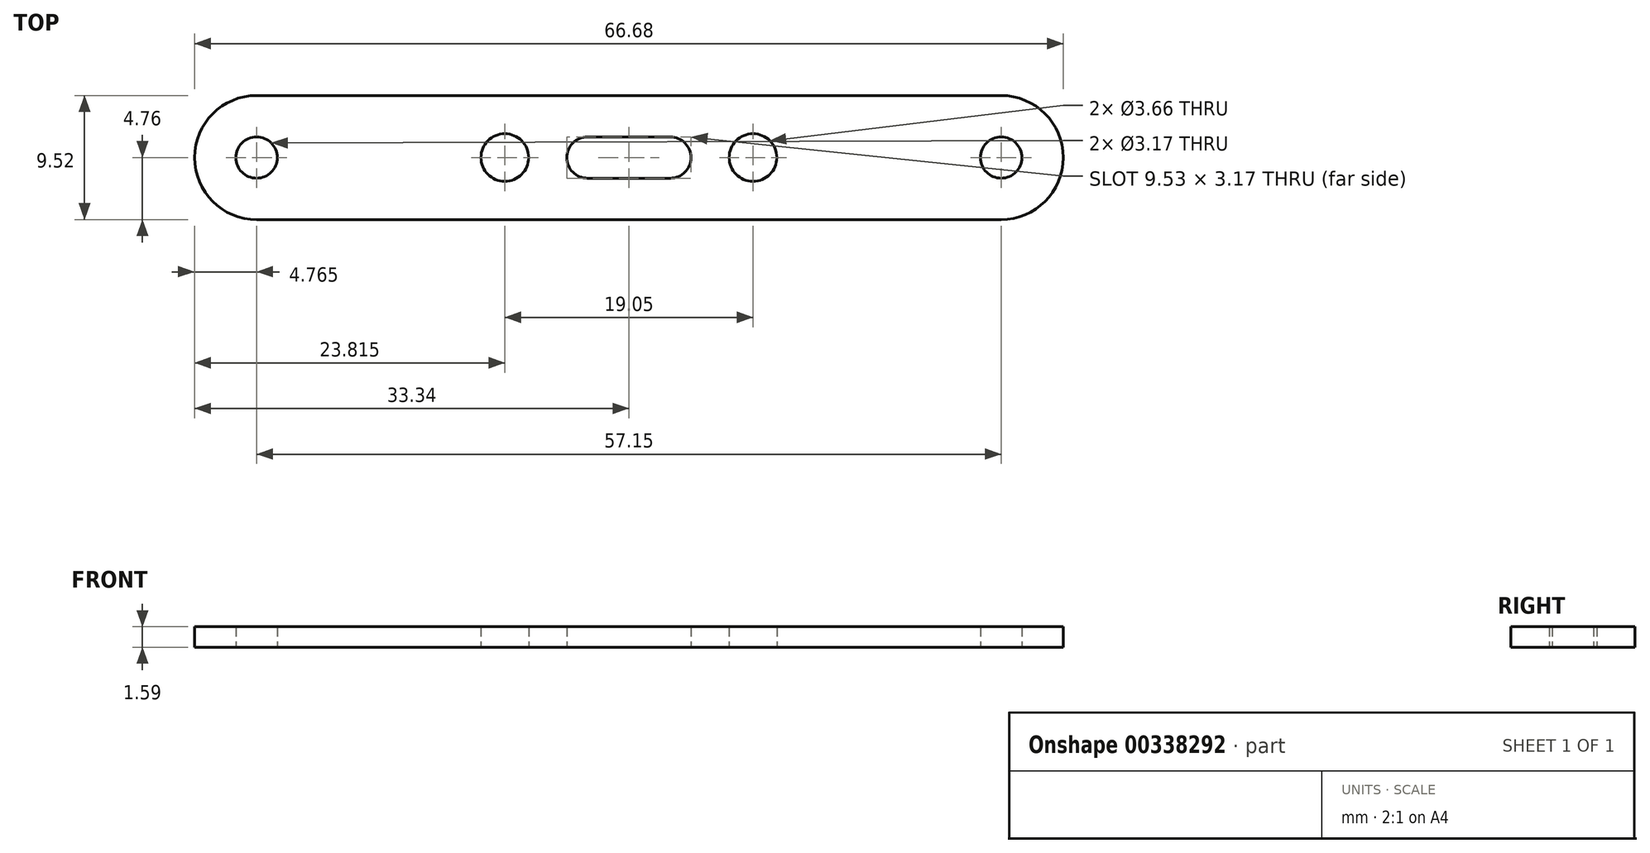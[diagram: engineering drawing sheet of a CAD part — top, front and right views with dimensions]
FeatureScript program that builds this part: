
annotation { "Feature Type Name" : "Feature", "Feature Type Description" : "" }
export const myFeature = defineFeature(function(context is Context, id is Id, definition is map)
    precondition{}
    {
        {
            var Q0;
            Q0=qCreatedBy(makeId("Top.planeOp"),FACE);
            var sketch = newSketch(context, id + "F0", { "sketchPlane" : qUnion([Q0])});
            skLineSegment(sketch, "E0.bottom", {"start": v(3.18, -1.59) * mm, "end": v(-3.18, -1.59) * mm});
            skLineSegment(sketch, "E0.top", {"start": v(3.18, 1.59) * mm, "end": v(-3.18, 1.59) * mm});
            skLineSegment(sketch, "E0.left", {"start": v(3.18, -1.59) * mm, "end": v(3.18, 1.59) * mm, "construction": true});
            skLineSegment(sketch, "E0.right", {"start": v(-3.18, -1.59) * mm, "end": v(-3.18, 1.59) * mm, "construction": true});
            skPoint(sketch, "E0.middle", {"position": v(0, 0) * mm});
            skArc(sketch, "E1", {"start": v(3.18, -1.59) * mm, "mid": v(4.76, 0) * mm, "end": v(3.18, 1.59) * mm});
            skArc(sketch, "E2", {"start": v(-3.18, 1.59) * mm, "mid": v(-4.76, 0) * mm, "end": v(-3.17, -1.59) * mm});
            skCircle(sketch, "E3", {"center": v(9.53, 0) * mm, "radius": 1.83 * mm});
            skLineSegment(sketch, "E4", {"start": v(-9.53, 0) * mm, "end": v(9.53, 0) * mm, "construction": true});
            skCircle(sketch, "E5", {"center": v(-9.53, 0) * mm, "radius": 1.83 * mm});
            skLineSegment(sketch, "E6", {"start": v(9.52, 0) * mm, "end": v(28.58, 0) * mm, "construction": true});
            skCircle(sketch, "E7", {"center": v(28.58, 0) * mm, "radius": 1.59 * mm});
            skLineSegment(sketch, "E8.bottom", {"start": v(28.58, 4.76) * mm, "end": v(-28.58, 4.76) * mm});
            skLineSegment(sketch, "E8.top", {"start": v(28.58, -4.76) * mm, "end": v(-28.58, -4.76) * mm});
            skLineSegment(sketch, "E8.left", {"start": v(28.58, 4.76) * mm, "end": v(28.58, -4.76) * mm, "construction": true});
            skLineSegment(sketch, "E8.right", {"start": v(-28.58, 4.76) * mm, "end": v(-28.58, -4.76) * mm, "construction": true});
            skLineSegment(sketch, "E9", {"start": v(-9.53, 0) * mm, "end": v(-28.58, 0) * mm, "construction": true});
            skArc(sketch, "E10", {"start": v(28.58, -4.76) * mm, "mid": v(33.34, 0) * mm, "end": v(28.58, 4.76) * mm});
            skArc(sketch, "E11", {"start": v(-28.58, 4.76) * mm, "mid": v(-33.34, 0) * mm, "end": v(-28.58, -4.76) * mm});
            skCircle(sketch, "E12", {"center": v(-28.58, 0) * mm, "radius": 1.59 * mm});
            skSolve(sketch);
        }
        {
            var Q0;
            Q0=qSketchRegion(id+"F0",true);
            extrude(context, id + "F1", {"entities" : qUnion([Q0]), "depth" : 1.59 * mm});
        }
    });
